# Revit family: Rohrschelle Sprinkler HDC, M12, Ø140-173
name_source: partatom
category: HLS-Bauteile
revit_build: Autodesk Revit 2017 (Build: 20190507_1515(x64)
units: mm (PartAtom-declared; Revit-internal decimal feet)

## family parameters
Arbeitsebenenbasiert = Ja
Beim Laden mit Abzugskörper schneiden = Nein
Bemaßung runder Anschluss = Durchmesser verwenden
Gemeinsam genutzt = Ja
Immer vertikal = Nein
Raumberechnungspunkt = Nein
Teiletyp = Normal

## types (2) — shared parameters
A = 18 mm  [stored 0.0590551 ft]
Anschluss = M12
Anschlußhöhe = 19 mm
Bauart = zweiteilig
DF1 = 30 mm  [stored 0.0984252 ft]
DVS = 10 mm  [stored 0.0328084 ft]
Fabrikat = Jiangmen Eurofix
Firma = MEFA Befestigungs- und Montagesysteme GmbH
H1 = 2 mm  [stored 0.00656168 ft]
HGA = 14 mm  [stored 0.0459318 ft]
Kurztext1 = Rohrschelle HDC 40x4
MB = 40 mm  [stored 0.131234 ft]
MD = 4 mm  [stored 0.0131234 ft]
Material = Stahl
Materialmaße = 40x4 mm
Mengeneinheit = St
Oberflaeche = galvanisch verzinkt
Verschluss-Schraube = M12
Vorgabe-Ansicht = 1219 mm
max. zul. Last = 5.00 kN
max. zul. Last horizontal = 0.00 kN
max. zul. Last vertikal = 0.00 kN
vpe = 10 St
zero-valued in all types: DS, Nennweite DN Rohr, Rohraußendurchmesser, Stärke Material

## per-type parameters (varying)
| type | AB | Achsabstand | Artikelnummer | B | Breite | D | D0 | DF2 | Dmax | Dmin | EAN | Gewicht | Gewicht pro Bauteil | H | H2 | Höhe | Kurztext2 | R | RM | Rohraußendurchmesser Zoll | S | max. Rohraußendurchmesser | min. Rohraußendurchmesser |
| RS Sprinkler HDC, M12, Ø140-148 | 8 mm  [stored 0.0262467 ft] | 186 mm | 47300140 | 216 mm  [stored 0.708661 ft] | 216 mm  [stored 0.708661 ft] | 148 mm  [stored 0.485564 ft] | 148 mm  [stored 0.485564 ft] | 30 mm  [stored 0.0984252 ft] | 148 mm  [stored 0.485564 ft] | 140 mm  [stored 0.459318 ft] | 4250928458292 | 0.81 kg | 0.81 kg | 170 mm  [stored 0.557743 ft] | 10 mm  [stored 0.0328084 ft] | 168 mm | 140 - 148 mm M12 | 74 mm  [stored 0.242782 ft] | 82 mm  [stored 0.269029 ft] | 5 Zoll | 186 mm  [stored 0.610236 ft] | 148 mm  [stored 0.485564 ft] | 140 mm  [stored 0.459318 ft] |
| RS Sprinkler HDC, M12, Ø167-173 | 1 mm  [stored 0.00328084 ft] | 212 mm | 47300167 | 242 mm  [stored 0.793963 ft] | 242 mm  [stored 0.793963 ft] | 168 mm  [stored 0.551181 ft] | 168 mm  [stored 0.551181 ft] | 31 mm  [stored 0.101706 ft] | 173 mm  [stored 0.567585 ft] | 167 mm  [stored 0.5479 ft] | 4250928458308 | 0.90 kg | 0.90 kg | 190 mm  [stored 0.62336 ft] | 6 mm  [stored 0.019685 ft] | 193 mm | 167 - 173 mm M12 | 84 mm  [stored 0.275591 ft] | 89 mm | 6 Zoll | 212 mm  [stored 0.695538 ft] | 173 mm  [stored 0.567585 ft] | 167 mm  [stored 0.5479 ft] |

note: [stored X ft] marks values corroborated as IEEE doubles in the binary element streams (Revit-internal decimal feet)

## geometry (parser evidence)
native form markers: Sweep x2
no freeform markers — native parametric forms only
